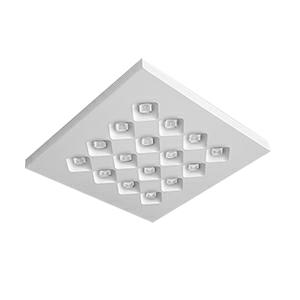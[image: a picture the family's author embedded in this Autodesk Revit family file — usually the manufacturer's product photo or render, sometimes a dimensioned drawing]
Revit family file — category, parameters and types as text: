
# Revit family: 3f_filippi_-_3f_diagon_soft_ugr_3f_filippi_-_23826_a0686_-_3f_diagon_25w-830_soft_ugr_596x596___corn_plaf__46c6
name_source: partatom
category: Lighting Fixtures
units: mm (PartAtom-declared; Revit-internal decimal feet)

## family parameters
Cut with Voids When Loaded = No
Host = Face
Light Source = No
Part Type = Normal
Room Calculation Point = No
Round Connector Dimension = Use Diameter
Shared = No

## types (1)
- 3F Filippi - 3F Dìagon Soft UGR (1 x LED, 3495 lm, 28 W, 3000 K)
    Apparent Load = 28 VA
    Approval mark = CE
    CIE Flux Codes = 59 92 100 100 100
    Color Rendering = 80
    Color Temperature = 3000 K
    Control Gear = Electronic ballast
    Default Elevation = 1800 mm
    Description = ILLUMINOTECHNICAL
Luminous efficiency 100% (DLOR 100%, ULOR 0%).
Initial luminous flux of the luminaire 3495 lm.
Direct symmetric distribution.
Installation Interdistance Transv.D = 1.23 x hu - Long.D = 1.23 x hu.
Average luminance <3000 cd/m² for radial angles >65°.
Tabular UGR (CIE 117 - 4H-8H; S=0.25H; 70/50/20): RUG 18.6 - 18.5.
Beam angle: 102° - 101°.
Luminous efficacy 125 lm/W.
Lifetime (L95/B10): 30000 h. (tq+25°C)
Lifetime (L90/B10): 50000 h. (tq+25°C)
Lifetime (L80/B10): 80000 h. (tq+25°C)
Lifetime (L75/B10): 100000 h. (tq+25°C)
Sudden decreased luminous flux after 50000 hours: 0% (C0).
Photobiological safety in compliance with IEC/TR 62778: RG0 risk exempt, (IEC 62471).
In compliance with IEC/EN 62722-2-1 - IEC/EN 62717 standards.

SOURCE
Squared LED module 25W/830.
Energy efficiency class (UE 2019/2020 - UE 2019/2015): C.
CIE 13.3 Colour rendering index: CRI >80 (R9 <50%).
IES TM-30 Fidelity Index: Rf = 84 Rg = 95.
CCT nominal colour temperature 3000 K.
Colour initial tolerance (MacAdam): SDCM 3.

MECHANICAL
Housing in hot-galvanised steel, painted in white polyester.
Honeycombed diagonal screen in white anti-glare polycarbonate.
Opal methacrylate (PMMA) rhomboid lenses with differentiated, engraved and prismatic surfaces for diffused, soft lighting and excellent visual comfort.
Luminaire with limited surface temperature. - D - (EN 60598-2-24)
Dimensions: 600x600 mm, height 40 mm. Weight 6.1 kg.
IP43 protection degree for exposed part, IP20 for recessed part.
Mechanical strength to impacts IK06 (1 joule).
Glow-wire test resistance 650°C.

ELECTRICAL
Halogen Free electronic wiring 230V-50/60Hz, power factor 0.95, THD <25%, constant output current, class I, 1 driver.
Power of the luminaire 28 W.
ENEC - CE.
SAFE FLICKER: PstLM=<1 and SVM=<0.4 (IEC TR 61547-1 and IEC TR 63158), to ensure a more comfortable and safe light.
Luminaire compliant with EN 60598-2-22 for power supply from a centralised emergency system CPSS (Central Power Supply System), not incorporated in the luminaire - high risk areas excluded. The default power and flux are 100% in AC and 100% in DC.
Ambient temperature from 0°C to +25°C.
Temperature class T6 max 85°C.
Quick connection.
Relative humidity UR: <85%.

INSTALLATION
Ceiling.
Height only 40 mm.
All accessories dedicated to this product are available on the Catalog and on our website www.3F-Filippi.com.

ACCESSORIES
A0686 - 596x596 Diagon frame for Ceiling installation.

APPLICATIONS
Environments: staterooms, with VDTs, offices.
Environments with exacting visual tasks, where diffused soft light for optimum visual comfort is required.

WARNING
Luminaire designed for disposal/recycling at end-of-life.
Replaceable (LED only) light source by a professional. Replaceable control gear by a professional.
    Height = 0 mm  [stored 0 ft]
    Lamp = 1 x LED
    Lamp Light Flux = 3495 lm
    Lamp Power = 28 W
    Lamp count = 1
    Length = 600 mm
    Lifetime = 50000 h
    Luminous efficacy = 125 lm/W
    Manufacturer = 3F Filippi
    ModVariant = No
    Model = 3F Filippi - 23826+A0686 - 3F Diagon 25W-830 SOFT UGR 596x596 + Corn.plaf.
    Mounting Place = Ceiling
    Mounting Type = Recessed
    Number of Poles = 1
    OnlyDefault = Yes
    Power Factor = 1
    Product Name = 3F Filippi - 3F Dìagon Soft UGR
    Product group = recessed luminaire
    ProductGroupID = 4
    Protection Class = Protection class I
    Protection Degree = IP 20
    RLX_Detail_Level = 1
    RLX_Emergency_Light_Flux = 0 lm
    RLX_Emergency_Type = 0
    RLX_Emergency_Type_DB = No
    RlxData = <blob elided: 96005 chars, md5=4bc34f71>
    Socket = socket
    Standby Power = 0 W
    System Light Flux = 3495 lm
    System Power = 28 W
    Type Comments = Product without accessories
    Type Image = 3ffilippi_3f_diagon__a0686.jpg
    URL = http://relux.com
    VarID = ---
    Voltage = 0 V
    Weight = 0.00 kg
    Width = 600 mm

note: [stored X ft] marks values corroborated as IEEE doubles in the binary element streams (Revit-internal decimal feet)

## geometry (parser evidence)
native form markers: Blend x4, Sweep x10
no freeform markers — native parametric forms only
